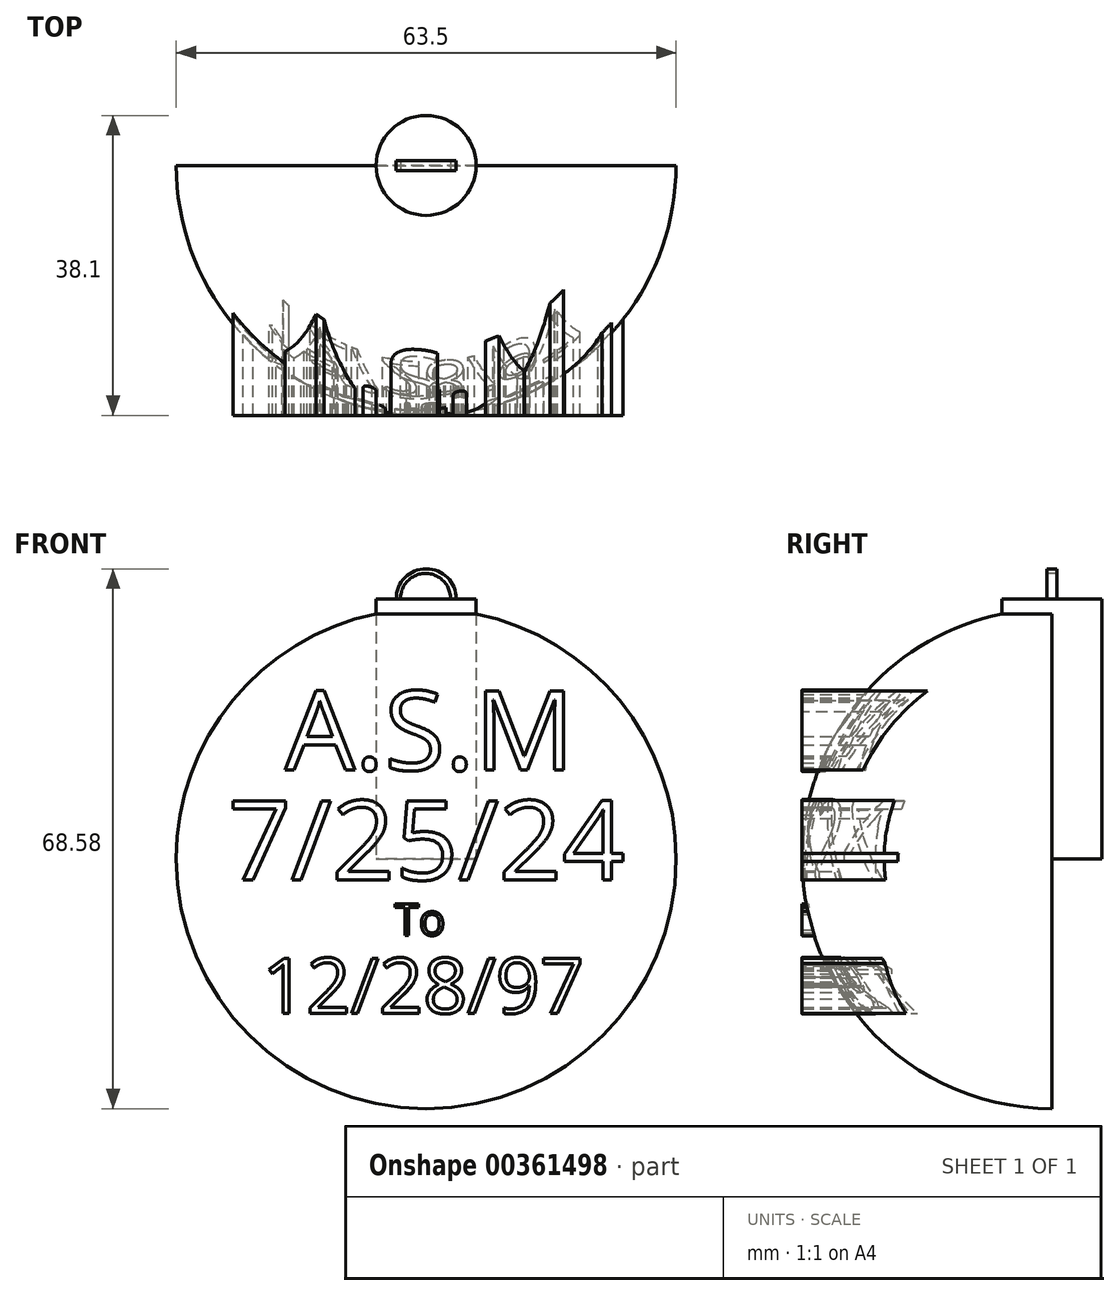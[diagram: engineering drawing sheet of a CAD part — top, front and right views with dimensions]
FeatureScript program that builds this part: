
annotation { "Feature Type Name" : "Feature", "Feature Type Description" : "" }
export const myFeature = defineFeature(function(context is Context, id is Id, definition is map)
    precondition{}
    {
        {
            var Q0;
            Q0=qCreatedBy(makeId("Front.planeOp"),FACE);
            var sketch = newSketch(context, id + "F0", { "sketchPlane" : qUnion([Q0])});
            skCircle(sketch, "E0", {"center": v(0, 0) * mm, "radius": 31.75 * mm});
            skLineSegment(sketch, "E1", {"start": v(-31.75, 0) * mm, "end": v(31.75, 0) * mm});
            skSolve(sketch);
        }
        {
            var Q0;
            {var subQ0=sQuery(id+"F0.wireOp",EDGE,"E1");Q0=makeQuery(id+"F0.imprint","IMPRINT",FACE,{"disambiguationData":[TD([[makeQuery(id+"F0.imprint","IMPRINT",EDGE,{"derivedFrom":subQ0}),-1.0]])]});}
            var Q1;
            Q1=sQuery(id+"F0.wireOp",EDGE,"E1");
            revolve(context, id + "F1", {"entities" : qUnion([Q0]), "axis" : qUnion([Q1]), "revolveType" : RevolveType.ONE_DIRECTION, "oppositeDirection" : true, "angle" : 180 * degree});
        }
        {
            var Q0;
            Q0=qCreatedBy(makeId("Front.planeOp"),FACE);
            var sketch = newSketch(context, id + "F2", { "sketchPlane" : qUnion([Q0])});
            skText(sketch, "E2", { "text": "A.S.M", "fontName": "OpenSans-Regular.ttf"});
            skText(sketch, "E3", { "text": "7/25/24\n", "fontName": "OpenSans-Regular.ttf"});
            skText(sketch, "E4", { "text": "To", "fontName": "OpenSans-Regular.ttf"});
            skText(sketch, "E5", { "text": "12/28/97", "fontName": "OpenSans-Regular.ttf"});
            const initialGuessF2  = {"E2": [-0.01795, 0.01127, 1, 0, 0.01012], "E3": [-0.0252, -0.00267, 1, 0, 0.01012], "E4": [-0.00401, -0.00974, 1, 0, 0.00401], "E5": [-0.02083, -0.01964, 1, 0, 0.00707]};
            skSetInitialGuess(sketch, initialGuessF2);
            skSolve(sketch);
        }
        {
            var Q0;
            Q0 = qSketchRegion(id + "F2", true);
            extrude(context, id + "F3", {"entities" : qUnion([Q0]), "operationType" : NewBodyOperationType.ADD, "depth" : 31.75 * mm});
        }
        {
            var Q0;
            Q0=qCreatedBy(makeId("Top.planeOp"),FACE);
            var sketch = newSketch(context, id + "F4", { "sketchPlane" : qUnion([Q0])});
            skCircle(sketch, "E6", {"center": v(0, 0) * mm, "radius": 6.35 * mm});
            skSolve(sketch);
        }
        {
            var Q0;
            Q0=makeQuery(id+"F4.imprint","IMPRINT",FACE,{"disambiguationData":[TD([[makeQuery(id+"F4.imprint","IMPRINT",EDGE,{"derivedFrom":sQuery(id+"F4.wireOp",EDGE,"E6")}),1.0]])]});
            extrude(context, id + "F5", {"entities" : qUnion([Q0]), "operationType" : NewBodyOperationType.ADD, "depth" : 33.02 * mm});
        }
        {
            var Q0;
            Q0=qCreatedBy(makeId("Front.planeOp"),FACE);
            var sketch = newSketch(context, id + "F6", { "sketchPlane" : qUnion([Q0])});
            skLineSegment(sketch, "E7.0", {"start": v(-6.35, 33.02) * mm, "end": v(6.35, 33.02) * mm});
            skLineSegment(sketch, "E8.0", {"start": v(-6.35, 31.1) * mm, "end": v(6.35, 31.1) * mm});
            skArc(sketch, "E9", {"start": v(3.81, 33.02) * mm, "mid": v(0, 36.83) * mm, "end": v(-3.81, 33.02) * mm});
            skSolve(sketch);
        }
        {
            var Q0;
            {var subQ0=sQuery(id+"F6.wireOp",EDGE,"E9");Q0=makeQuery(id+"F6.imprint","IMPRINT",FACE,{"disambiguationData":[TD([[makeQuery(id+"F6.imprint","IMPRINT",EDGE,{"derivedFrom":subQ0}),1.0]])]});}
            extrude(context, id + "F7", {"entities" : qUnion([Q0]), "operationType" : NewBodyOperationType.ADD, "endBound" : BoundingType.SYMMETRIC, "oppositeDirection" : true, "depth" : 1.27 * mm});
        }
        {
            var Q0;
            Q0=qCreatedBy(makeId("Front.planeOp"),FACE);
            var sketch = newSketch(context, id + "F8", { "sketchPlane" : qUnion([Q0])});
            skLineSegment(sketch, "E10.0", {"start": v(-6.35, 33.02) * mm, "end": v(6.35, 33.02) * mm});
            skLineSegment(sketch, "E11.0", {"start": v(-6.35, 31.1) * mm, "end": v(6.35, 31.1) * mm});
            skArc(sketch, "E12", {"start": v(3.1, 33.02) * mm, "mid": v(-0.08, 36.25) * mm, "end": v(-3.25, 33.02) * mm});
            skSolve(sketch);
        }
        {
            var Q0;
            Q0 = qSketchRegion(id + "F8", true);
            extrude(context, id + "F9", {"entities" : qUnion([Q0]), "operationType" : NewBodyOperationType.REMOVE, "endBound" : BoundingType.THROUGH_ALL, "oppositeDirection" : true, "depth" : 50.8 * mm});
        }
        {
            var Q0;
            Q0 = qSketchRegion(id + "F8", true);
            extrude(context, id + "F10", {"entities" : qUnion([Q0]), "operationType" : NewBodyOperationType.REMOVE, "depth" : 25.4 * mm});
        }
    });
